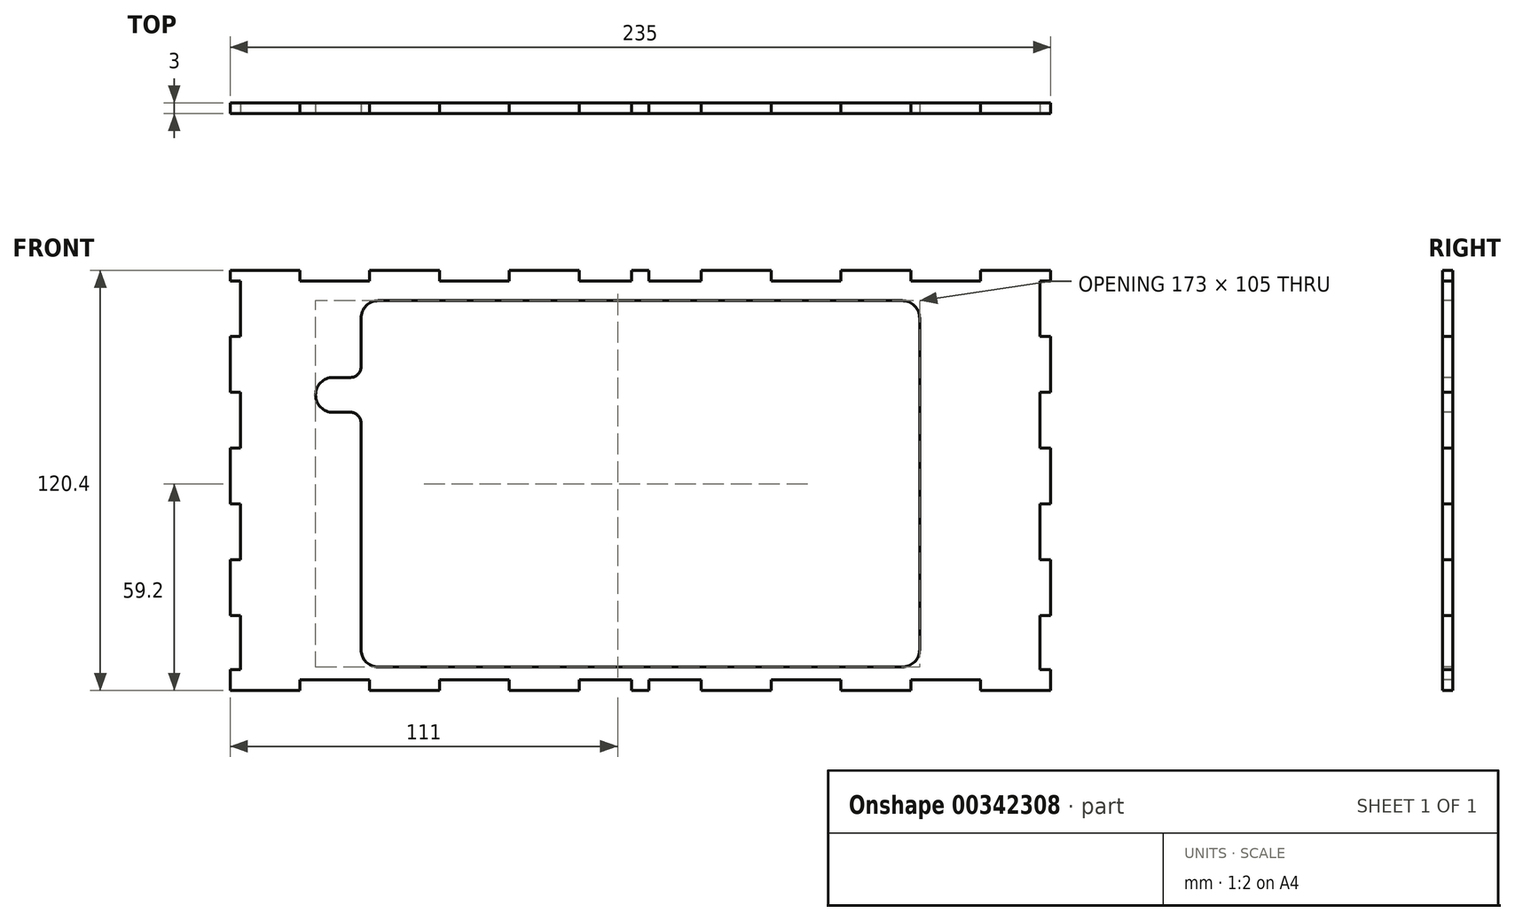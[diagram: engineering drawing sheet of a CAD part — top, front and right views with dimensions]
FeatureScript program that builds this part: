
annotation { "Feature Type Name" : "Feature", "Feature Type Description" : "" }
export const myFeature = defineFeature(function(context is Context, id is Id, definition is map)
    precondition{}
    {
        {
            var Q0;
            Q0=qCreatedBy(makeId("Front.planeOp"),FACE);
            var sketch = newSketch(context, id + "F0", { "sketchPlane" : qUnion([Q0])});
            skLineSegment(sketch, "E0.bottom", {"start": v(5, 0) * mm, "end": v(155, 0) * mm});
            skLineSegment(sketch, "E0.top", {"start": v(5, 105) * mm, "end": v(155, 105) * mm});
            skLineSegment(sketch, "E0.right", {"start": v(160, 5) * mm, "end": v(160, 100) * mm});
            skLineSegment(sketch, "E1", {"start": v(0, 100) * mm, "end": v(0, 86) * mm});
            skLineSegment(sketch, "E2", {"start": v(0, 70) * mm, "end": v(0, 5) * mm});
            skLineSegment(sketch, "E3", {"start": v(-13, 78) * mm, "end": v(-8, 78) * mm, "construction": true});
            skArc(sketch, "E4", {"start": v(-8, 73) * mm, "mid": v(-13, 78) * mm, "end": v(-8, 83) * mm});
            skLineSegment(sketch, "E5", {"start": v(-8, 83) * mm, "end": v(-3, 83) * mm});
            skLineSegment(sketch, "E6", {"start": v(-3, 73) * mm, "end": v(-8, 73) * mm});
            skPoint(sketch, "E7.visualSharp", {"position": v(0, 105) * mm});
            skArc(sketch, "E7.filletArc", {"start": v(5, 105) * mm, "mid": v(1.46, 103.54) * mm, "end": v(0, 100) * mm});
            skPoint(sketch, "E8.visualSharp", {"position": v(160, 105) * mm});
            skArc(sketch, "E8.filletArc", {"start": v(160, 100) * mm, "mid": v(158.54, 103.54) * mm, "end": v(155, 105) * mm});
            skPoint(sketch, "E9.visualSharp", {"position": v(160, 0) * mm});
            skArc(sketch, "E9.filletArc", {"start": v(155, 0) * mm, "mid": v(158.54, 1.46) * mm, "end": v(160, 5) * mm});
            skPoint(sketch, "E10.visualSharp", {"position": v(0, 0) * mm});
            skArc(sketch, "E10.filletArc", {"start": v(0, 5) * mm, "mid": v(1.46, 1.46) * mm, "end": v(5, 0) * mm});
            skPoint(sketch, "E11.visualSharp", {"position": v(0, 83) * mm});
            skArc(sketch, "E11.filletArc", {"start": v(-3, 83) * mm, "mid": v(-0.88, 83.88) * mm, "end": v(0, 86) * mm});
            skPoint(sketch, "E12.visualSharp", {"position": v(0, 73) * mm});
            skArc(sketch, "E12.filletArc", {"start": v(0, 70) * mm, "mid": v(-0.88, 72.12) * mm, "end": v(-3, 73) * mm});
            skLineSegment(sketch, "E13", {"start": v(-17.5, 113.7) * mm, "end": v(-17.5, 110.7) * mm});
            skLineSegment(sketch, "E14", {"start": v(-37.5, 110.7) * mm, "end": v(-17.5, 110.7) * mm, "construction": true});
            skLineSegment(sketch, "E15", {"start": v(-17.5, 110.7) * mm, "end": v(2.5, 110.7) * mm});
            skLineSegment(sketch, "E16", {"start": v(2.5, 110.7) * mm, "end": v(2.5, 113.7) * mm});
            skLineSegment(sketch, "E17", {"start": v(2.5, 113.7) * mm, "end": v(22.5, 113.7) * mm});
            skLineSegment(sketch, "E18", {"start": v(22.5, 113.7) * mm, "end": v(22.5, 110.7) * mm});
            skLineSegment(sketch, "E19", {"start": v(22.5, 110.7) * mm, "end": v(42.5, 110.7) * mm});
            skLineSegment(sketch, "E20", {"start": v(42.5, 110.7) * mm, "end": v(42.5, 113.7) * mm});
            skLineSegment(sketch, "E21", {"start": v(42.5, 113.7) * mm, "end": v(62.5, 113.7) * mm});
            skLineSegment(sketch, "E22", {"start": v(62.5, 113.7) * mm, "end": v(62.5, 110.7) * mm});
            skLineSegment(sketch, "E23", {"start": v(97.5, 110.7) * mm, "end": v(97.5, 113.7) * mm});
            skLineSegment(sketch, "E24", {"start": v(97.5, 113.7) * mm, "end": v(117.5, 113.7) * mm});
            skLineSegment(sketch, "E25", {"start": v(117.5, 113.7) * mm, "end": v(117.5, 110.7) * mm});
            skLineSegment(sketch, "E26", {"start": v(-37.5, 113.7) * mm, "end": v(-17.5, 113.7) * mm});
            skLineSegment(sketch, "E27", {"start": v(117.5, 110.7) * mm, "end": v(137.5, 110.7) * mm});
            skLineSegment(sketch, "E28", {"start": v(137.5, 110.7) * mm, "end": v(137.5, 113.7) * mm});
            skLineSegment(sketch, "E29", {"start": v(137.5, 113.7) * mm, "end": v(157.5, 113.7) * mm});
            skLineSegment(sketch, "E30", {"start": v(157.5, 113.7) * mm, "end": v(157.5, 110.7) * mm});
            skLineSegment(sketch, "E31", {"start": v(157.5, 110.7) * mm, "end": v(177.5, 110.7) * mm});
            skLineSegment(sketch, "E32", {"start": v(177.5, 110.7) * mm, "end": v(177.5, 113.7) * mm});
            skLineSegment(sketch, "E33", {"start": v(177.5, 113.7) * mm, "end": v(197.5, 113.7) * mm});
            skLineSegment(sketch, "E34", {"start": v(197.5, 113.7) * mm, "end": v(197.5, 110.7) * mm});
            skLineSegment(sketch, "E35", {"start": v(197.5, 110.7) * mm, "end": v(194.5, 110.7) * mm});
            skLineSegment(sketch, "E36", {"start": v(194.5, 110.7) * mm, "end": v(194.5, 94.7) * mm});
            skLineSegment(sketch, "E37", {"start": v(194.5, 94.7) * mm, "end": v(197.5, 94.7) * mm});
            skLineSegment(sketch, "E38", {"start": v(197.5, 94.7) * mm, "end": v(197.5, 78.7) * mm});
            skLineSegment(sketch, "E39", {"start": v(197.5, 78.7) * mm, "end": v(194.5, 78.7) * mm});
            skLineSegment(sketch, "E40", {"start": v(194.5, 78.7) * mm, "end": v(194.5, 62.7) * mm});
            skLineSegment(sketch, "E41", {"start": v(194.5, 62.7) * mm, "end": v(197.5, 62.7) * mm});
            skLineSegment(sketch, "E42", {"start": v(197.5, 62.7) * mm, "end": v(197.5, 46.7) * mm});
            skLineSegment(sketch, "E43", {"start": v(197.5, 46.7) * mm, "end": v(194.5, 46.7) * mm});
            skLineSegment(sketch, "E44", {"start": v(194.5, 46.7) * mm, "end": v(194.5, 30.7) * mm});
            skLineSegment(sketch, "E45", {"start": v(194.5, 30.7) * mm, "end": v(197.5, 30.7) * mm});
            skLineSegment(sketch, "E46", {"start": v(197.5, 30.7) * mm, "end": v(197.5, 14.7) * mm});
            skLineSegment(sketch, "E47", {"start": v(197.5, 14.7) * mm, "end": v(194.5, 14.7) * mm});
            skLineSegment(sketch, "E48", {"start": v(-37.5, 113.7) * mm, "end": v(-37.5, 110.7) * mm});
            skLineSegment(sketch, "E49", {"start": v(-37.5, 110.7) * mm, "end": v(-34.5, 110.7) * mm});
            skLineSegment(sketch, "E50", {"start": v(-34.5, 110.7) * mm, "end": v(-34.5, 94.7) * mm});
            skLineSegment(sketch, "E51", {"start": v(-34.5, 94.7) * mm, "end": v(-37.5, 94.7) * mm});
            skLineSegment(sketch, "E52", {"start": v(-37.5, 94.7) * mm, "end": v(-37.5, 78.7) * mm});
            skLineSegment(sketch, "E53", {"start": v(-37.5, 78.7) * mm, "end": v(-34.5, 78.7) * mm});
            skLineSegment(sketch, "E54", {"start": v(-34.5, 78.7) * mm, "end": v(-34.5, 62.7) * mm});
            skLineSegment(sketch, "E55", {"start": v(-34.5, 62.7) * mm, "end": v(-37.5, 62.7) * mm});
            skLineSegment(sketch, "E56", {"start": v(-37.5, 62.7) * mm, "end": v(-37.5, 46.7) * mm});
            skLineSegment(sketch, "E57", {"start": v(-37.5, 46.7) * mm, "end": v(-34.5, 46.7) * mm});
            skLineSegment(sketch, "E58", {"start": v(-34.5, 46.7) * mm, "end": v(-34.5, 30.7) * mm});
            skLineSegment(sketch, "E59", {"start": v(-34.5, 30.7) * mm, "end": v(-37.5, 30.7) * mm});
            skLineSegment(sketch, "E60", {"start": v(-37.5, 30.7) * mm, "end": v(-37.5, 14.7) * mm});
            skLineSegment(sketch, "E61", {"start": v(-37.5, 14.7) * mm, "end": v(-34.5, 14.7) * mm});
            skLineSegment(sketch, "E62", {"start": v(80, 51.44) * mm, "end": v(-37.5, 51.44) * mm, "construction": true});
            skLineSegment(sketch, "E63", {"start": v(80, 51.44) * mm, "end": v(197.5, 51.44) * mm, "construction": true});
            skLineSegment(sketch, "E64", {"start": v(80, 51.44) * mm, "end": v(80, 112.94) * mm, "construction": true});
            skLineSegment(sketch, "E65", {"start": v(80, 51.44) * mm, "end": v(80, 0) * mm, "construction": true});
            skLineSegment(sketch, "E66", {"start": v(194.5, 14.7) * mm, "end": v(194.5, -0.7) * mm});
            skLineSegment(sketch, "E67", {"start": v(194.5, -0.7) * mm, "end": v(197.5, -0.7) * mm});
            skLineSegment(sketch, "E68", {"start": v(197.5, -0.7) * mm, "end": v(197.5, -6.7) * mm});
            skLineSegment(sketch, "E69", {"start": v(-34.5, 14.7) * mm, "end": v(-34.5, -0.7) * mm});
            skLineSegment(sketch, "E70", {"start": v(-34.5, -0.7) * mm, "end": v(-37.5, -0.7) * mm});
            skLineSegment(sketch, "E71", {"start": v(-37.5, -0.7) * mm, "end": v(-37.5, -6.7) * mm});
            skLineSegment(sketch, "E72", {"start": v(82.5, 110.7) * mm, "end": v(82.5, 113.7) * mm});
            skLineSegment(sketch, "E73", {"start": v(77.5, 110.7) * mm, "end": v(77.5, 113.7) * mm});
            skLineSegment(sketch, "E74", {"start": v(77.5, 113.7) * mm, "end": v(82.5, 113.7) * mm});
            skLineSegment(sketch, "E75", {"start": v(-37.5, -6.7) * mm, "end": v(-17.5, -6.7) * mm});
            skLineSegment(sketch, "E76", {"start": v(-17.5, -6.7) * mm, "end": v(-17.5, -3.7) * mm});
            skLineSegment(sketch, "E77", {"start": v(-17.5, -3.7) * mm, "end": v(2.5, -3.7) * mm});
            skLineSegment(sketch, "E78", {"start": v(2.5, -3.7) * mm, "end": v(2.5, -6.7) * mm});
            skLineSegment(sketch, "E79", {"start": v(2.5, -6.7) * mm, "end": v(22.5, -6.7) * mm});
            skLineSegment(sketch, "E80", {"start": v(22.5, -6.7) * mm, "end": v(22.5, -3.7) * mm});
            skLineSegment(sketch, "E81", {"start": v(22.5, -3.7) * mm, "end": v(42.5, -3.7) * mm});
            skLineSegment(sketch, "E82", {"start": v(42.5, -3.7) * mm, "end": v(42.5, -6.7) * mm});
            skLineSegment(sketch, "E83", {"start": v(42.5, -6.7) * mm, "end": v(62.5, -6.7) * mm});
            skLineSegment(sketch, "E84", {"start": v(62.5, -6.7) * mm, "end": v(62.5, -3.7) * mm});
            skLineSegment(sketch, "E85", {"start": v(82.5, -3.7) * mm, "end": v(82.5, -6.7) * mm});
            skLineSegment(sketch, "E86", {"start": v(77.5, -6.7) * mm, "end": v(82.5, -6.7) * mm});
            skLineSegment(sketch, "E87", {"start": v(77.5, -6.7) * mm, "end": v(77.5, -3.7) * mm});
            skLineSegment(sketch, "E88", {"start": v(97.5, -3.7) * mm, "end": v(97.5, -6.7) * mm});
            skLineSegment(sketch, "E89", {"start": v(97.5, -6.7) * mm, "end": v(117.5, -6.7) * mm});
            skLineSegment(sketch, "E90", {"start": v(117.5, -6.7) * mm, "end": v(117.5, -3.7) * mm});
            skLineSegment(sketch, "E91", {"start": v(117.5, -3.7) * mm, "end": v(137.5, -3.7) * mm});
            skLineSegment(sketch, "E92", {"start": v(137.5, -3.7) * mm, "end": v(137.5, -6.7) * mm});
            skLineSegment(sketch, "E93", {"start": v(137.5, -6.7) * mm, "end": v(157.5, -6.7) * mm});
            skLineSegment(sketch, "E94", {"start": v(157.5, -6.7) * mm, "end": v(157.5, -3.7) * mm});
            skLineSegment(sketch, "E95", {"start": v(157.5, -3.7) * mm, "end": v(177.5, -3.7) * mm});
            skLineSegment(sketch, "E96", {"start": v(177.5, -3.7) * mm, "end": v(177.5, -6.7) * mm});
            skLineSegment(sketch, "E97", {"start": v(177.5, -6.7) * mm, "end": v(197.5, -6.7) * mm});
            skLineSegment(sketch, "E98", {"start": v(82.5, -3.7) * mm, "end": v(97.5, -3.7) * mm});
            skLineSegment(sketch, "E99", {"start": v(62.5, -3.7) * mm, "end": v(77.5, -3.7) * mm});
            skLineSegment(sketch, "E100", {"start": v(62.5, 110.7) * mm, "end": v(77.5, 110.7) * mm});
            skLineSegment(sketch, "E101", {"start": v(82.5, 110.7) * mm, "end": v(97.5, 110.7) * mm});
            skSolve(sketch);
        }
        {
            var Q0;
            Q0=makeQuery(id+"F0.imprint","IMPRINT",FACE,{"disambiguationData":[TD([[makeQuery(id+"F0.imprint","IMPRINT",EDGE,{"derivedFrom":sQuery(id+"F0.wireOp",EDGE,"E0.bottom")}),-1.0]])]});
            extrude(context, id + "F1", {"entities" : qUnion([Q0]), "oppositeDirection" : true, "offsetDistance" : 25 * mm, "depth" : 3 * mm});
        }
    });
